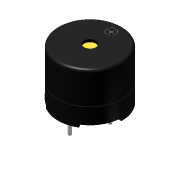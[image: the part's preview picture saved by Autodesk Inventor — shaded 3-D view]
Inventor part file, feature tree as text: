
AUTODESK INVENTOR PART (.ipt)
format: ipt  version: 2012 (Build 160160000, 160)  size: 194,560 bytes
history: native  units: mm
features: extrude x10, sketch x10, plane x2, fillet x1, pattern_circular x1, chamfer x1, projected_geometry x1
ambient origin geometry x8: Origin, YZ Plane, XZ Plane, XY Plane, X Axis, Y Axis, Z Axis, Center Point
bodies: Solid1 (feature_tree)
feature tree (26):
  extrude  "Extrusion1"  Depth=9.5mm TaperAngle=0.0deg
  plane  "Work Plane1"
  extrude  "Extrusion2"  Depth=8.5mm
  extrude  "Extrusion3"  Depth=2.2mm
  extrude  "Extrusion4"  Depth=10.5mm
  fillet  "Fillet1"  Radius=0.5mm
  extrude  "Extrusion5"  Depth=0.5mm TaperAngle=0.0deg
  pattern_circular  "Circular Pattern1"  Count=3 Angle=360.0deg
  extrude  "Extrusion6"  Depth=3.8mm
  extrude  "Extrusion7"  Depth=0.6mm
  chamfer  "Chamfer1"  Distance=4.0mm
  extrude  "Extrusion8"  Depth=0.1mm TaperAngle=0.0deg
  extrude  "Extrusion9"  [1 undecoded]
  plane  "Work Plane2"
  extrude  "Extrusion10"  Depth=11.5mm
  sketch  "Sketch1"  dims[d0=12.0mm d1=9.5mm d2=0.0mm]
  sketch  "Sketch2"  dims[d3=-0.5mm d4=8.5mm]
  projected_geometry  "Projected Loop1"
  sketch  "Sketch3"  dims[d5=1.0mm d6=0.0mm d7=2.2mm]
  sketch  "Sketch4"  dims[d8=0.5mm d9=0.0mm d10=10.5mm d11=0.5mm d12=0.0mm]
  sketch  "Sketch5"  dims[d13=0.5mm d14=0.5mm d15=0.0mm d16=30.0mm d17=360.0deg]
  sketch  "Sketch6"  dims[d19=0.6mm d20=3.8mm]
  sketch  "Sketch7"  dims[d21=6.0mm d22=0.0mm d23=0.6mm]
  sketch  "Sketch8"  dims[d24=3.8mm d25=4.0mm d26=0.0mm]
  sketch  "Sketch9"  dims[d27=0.2mm d28=2.0mm d29=45.0deg d30=0.1mm d31=0.0mm]
  sketch  "Sketch10"  dims[d32=0.01mm d33=0.0mm d34=-6.0mm d35=11.5mm d36=0.1mm d37=0.0mm]
note: 1 required parameter value undecoded (feature->parameter linkage not recoverable at this tier; creation-order binding heuristic only, values carry confidence <= 0.55)
